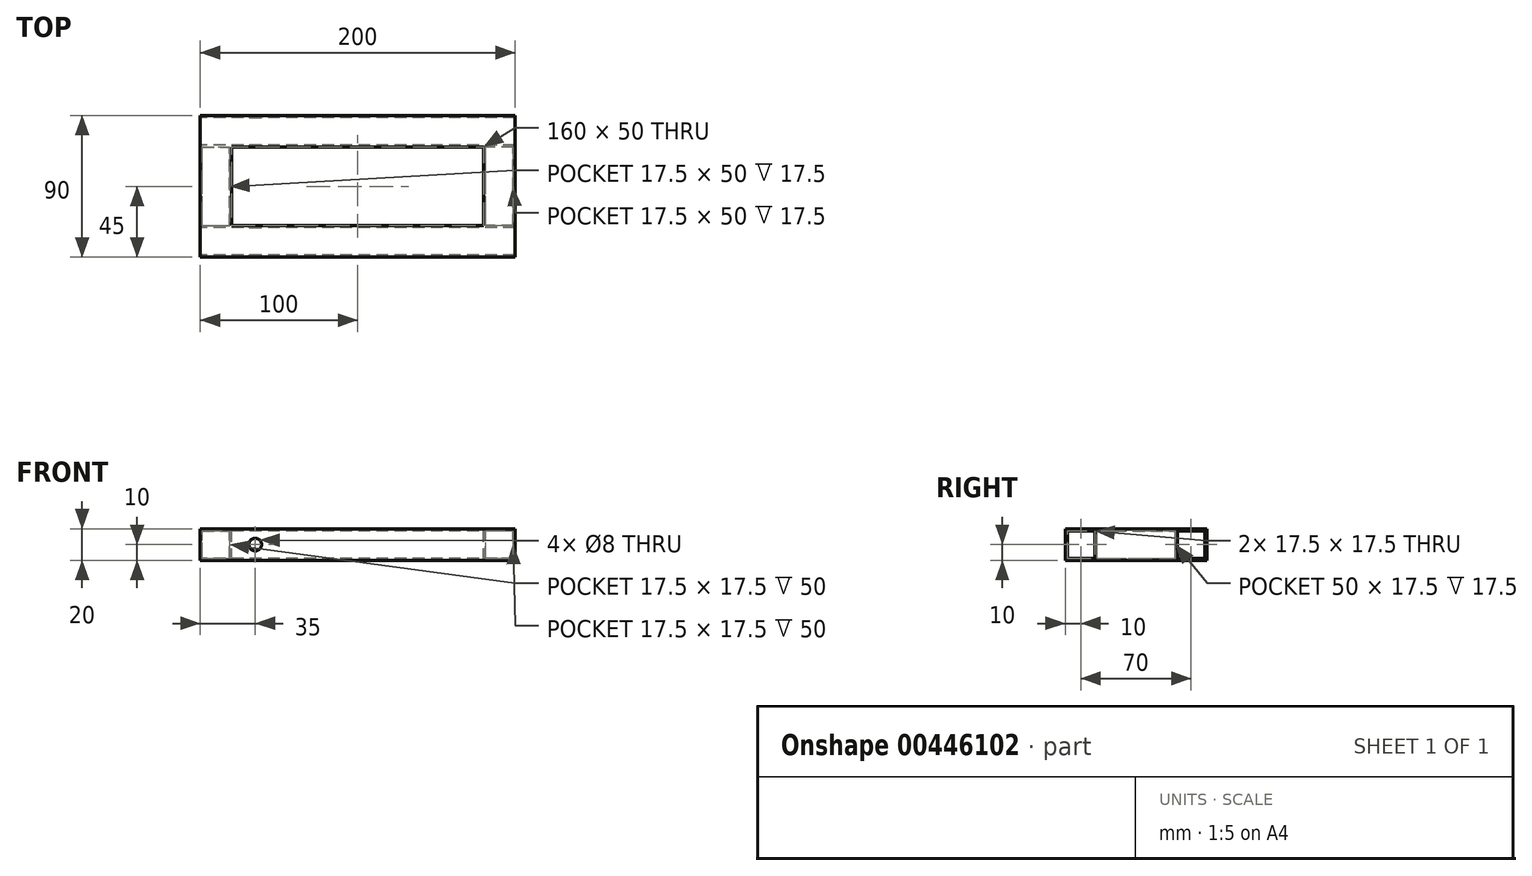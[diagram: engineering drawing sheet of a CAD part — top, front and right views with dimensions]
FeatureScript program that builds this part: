
annotation { "Feature Type Name" : "Feature", "Feature Type Description" : "" }
export const myFeature = defineFeature(function(context is Context, id is Id, definition is map)
    precondition{}
    {
        {
            var Q0;
            Q0=qCreatedBy(makeId("Right.planeOp"),FACE);
            var sketch = newSketch(context, id + "F0", { "sketchPlane" : qUnion([Q0])});
            skLineSegment(sketch, "E0.bottom", {"start": v(0, 0) * mm, "end": v(20, 0) * mm});
            skLineSegment(sketch, "E0.top", {"start": v(0, 20) * mm, "end": v(20, 20) * mm});
            skLineSegment(sketch, "E0.left", {"start": v(0, 0) * mm, "end": v(0, 20) * mm});
            skLineSegment(sketch, "E0.right", {"start": v(20, 0) * mm, "end": v(20, 20) * mm});
            skLineSegment(sketch, "E1.0", {"start": v(1.25, 18.75) * mm, "end": v(18.75, 18.75) * mm});
            skLineSegment(sketch, "E1.1", {"start": v(1.25, 1.25) * mm, "end": v(1.25, 18.75) * mm});
            skLineSegment(sketch, "E1.2", {"start": v(1.25, 1.25) * mm, "end": v(18.75, 1.25) * mm});
            skLineSegment(sketch, "E1.3", {"start": v(18.75, 1.25) * mm, "end": v(18.75, 18.75) * mm});
            skSolve(sketch);
        }
        {
            var Q0;
            Q0 = qSketchRegion(id + "F0", true);
            extrude(context, id + "F1", {"entities" : qUnion([Q0]), "depth" : 200 * mm});
        }
        {
            var Q0;
            Q0=makeQuery(id+"F1.opExtrude","SWEPT_FACE",FACE,{"disambiguationData":[OSD([sQuery(id+"F0.wireOp",EDGE,"E0.left")])]});
            var sketch = newSketch(context, id + "F2", { "sketchPlane" : qUnion([Q0])});
            skLineSegment(sketch, "E2.bottom", {"start": v(0, 0) * mm, "end": v(20, 0) * mm});
            skLineSegment(sketch, "E2.top", {"start": v(0, 20) * mm, "end": v(20, 20) * mm});
            skLineSegment(sketch, "E2.left", {"start": v(0, 0) * mm, "end": v(0, 20) * mm});
            skLineSegment(sketch, "E2.right", {"start": v(20, 0) * mm, "end": v(20, 20) * mm});
            skLineSegment(sketch, "E3.bottom", {"start": v(200, 0) * mm, "end": v(180, 0) * mm});
            skLineSegment(sketch, "E3.top", {"start": v(200, 20) * mm, "end": v(180, 20) * mm});
            skLineSegment(sketch, "E3.left", {"start": v(200, 0) * mm, "end": v(200, 20) * mm});
            skLineSegment(sketch, "E3.right", {"start": v(180, 0) * mm, "end": v(180, 20) * mm});
            skLineSegment(sketch, "E4.0", {"start": v(1.25, 18.75) * mm, "end": v(18.75, 18.75) * mm});
            skLineSegment(sketch, "E4.1", {"start": v(1.25, 1.25) * mm, "end": v(1.25, 18.75) * mm});
            skLineSegment(sketch, "E4.2", {"start": v(1.25, 1.25) * mm, "end": v(18.75, 1.25) * mm});
            skLineSegment(sketch, "E4.3", {"start": v(18.75, 1.25) * mm, "end": v(18.75, 18.75) * mm});
            skLineSegment(sketch, "E5.0", {"start": v(198.75, 18.75) * mm, "end": v(181.25, 18.75) * mm});
            skLineSegment(sketch, "E5.1", {"start": v(198.75, 1.25) * mm, "end": v(198.75, 18.75) * mm});
            skLineSegment(sketch, "E5.2", {"start": v(198.75, 1.25) * mm, "end": v(181.25, 1.25) * mm});
            skLineSegment(sketch, "E5.3", {"start": v(181.25, 1.25) * mm, "end": v(181.25, 18.75) * mm});
            skSolve(sketch);
        }
        {
            var Q0;
            Q0 = qSketchRegion(id + "F2", true);
            extrude(context, id + "F3", {"entities" : qUnion([Q0]), "operationType" : NewBodyOperationType.ADD, "depth" : 50 * mm});
        }
        {
            var Q0;
            Q0=makeQuery(id+"F3.boolean.opBoolean","SPLIT",FACE,{"disambiguationData":[TD([makeQuery(id+"F1.opExtrude","SWEPT_FACE",FACE,{"disambiguationData":[OSD([sQuery(id+"F0.wireOp",EDGE,"E0.bottom")])]})])],"derivedFrom":makeQuery(id+"F1.opExtrude","SWEPT_FACE",FACE,{"disambiguationData":[OSD([sQuery(id+"F0.wireOp",EDGE,"E0.left")])]})});
            var sketch = newSketch(context, id + "F4", { "sketchPlane" : qUnion([Q0])});
            skLineSegment(sketch, "E6", {"start": v(20, 10) * mm, "end": v(180, 10) * mm, "construction": true});
            skCircle(sketch, "E7", {"center": v(35, 10) * mm, "radius": 4 * mm});
            skSolve(sketch);
        }
        {
            var Q0;
            Q0 = qSketchRegion(id + "F4", true);
            extrude(context, id + "F5", {"entities" : qUnion([Q0]), "operationType" : NewBodyOperationType.REMOVE, "endBound" : BoundingType.THROUGH_ALL, "oppositeDirection" : true, "depth" : 25 * mm});
        }
        {
            var Q0;
            Q0=makeQuery(id+"F3.opExtrude","SWEPT_EDGE",EDGE,{"disambiguationData":[OSD([sQuery(id+"F0.wireOp",EDGE,"E0.top"),sQuery(id+"F0.wireOp",EDGE,"E0.left"),sQuery(id+"F2.wireOp",EDGE,"E3.top"),sQuery(id+"F2.wireOp",EDGE,"E3.right")])]});
            cPoint(context, id + "F6", {"entities" : qUnion([Q0]), "parameter" : 0.5});
        }
        {
            var Q0;
            Q0=qCreatedBy(makeId("Front.planeOp"),FACE);
            var Q1;
            Q1 = qCreatedBy(id + "F6" ,VERTEX);
            cPlane(context, id + "F7", {"entities" : qUnion([Q0, Q1]), "cplaneType" : CPlaneType.PLANE_POINT, "offset" : 25 * mm, "width" : 150 * mm, "height" : 150 * mm});
        }
        {
            var Q0;
            Q0=makeQuery(id+"F1.opExtrude","SWEPT_BODY",BODY,{"disambiguationData":[OSD([sQuery(id+"F0.wireOp",EDGE,"E0.bottom"),sQuery(id+"F0.wireOp",EDGE,"E0.top"),sQuery(id+"F0.wireOp",EDGE,"E0.left"),sQuery(id+"F0.wireOp",EDGE,"E0.right"),sQuery(id+"F0.wireOp",EDGE,"E1.0"),sQuery(id+"F0.wireOp",EDGE,"E1.1"),sQuery(id+"F0.wireOp",EDGE,"E1.2"),sQuery(id+"F0.wireOp",EDGE,"E1.3")])]});
            var Q1;
            Q1=qCreatedBy(id+"F7.planeOp",FACE);
            mirror(context, id + "F8", {"operationType" : NewBodyOperationType.ADD, "entities" : qUnion([Q0]), "mirrorPlane" : qUnion([Q1])});
        }
    });
